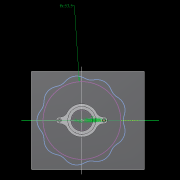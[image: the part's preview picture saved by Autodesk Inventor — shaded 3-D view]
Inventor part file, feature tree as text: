
AUTODESK INVENTOR PART (.ipt)
format: ipt  version: 2022.2 (Build 262287010, 287A)  size: 509,440 bytes
history: native  units: mm
features: other x19, extrude x14, sketch x9, pattern_circular x7, fillet x2, move_body x2, revolve x2, draft x2, plane x2
ambient origin geometry x8: Origin, YZ Plane, XZ Plane, XY Plane, X Axis, Y Axis, Z Axis, Center Point
bodies: Solid5 (feature_tree)
feature tree (59):
  other  "CrossSection1"
  sketch  "Sketch7"  dims[d90=16.297397mm]
  other  "Roller1"
  other  "Roller2"
  sketch  "Sketch22"  dims[d167=8.972256mm]
  sketch  "Sketch2"  dims[d57=4.025mm]
  sketch  "Sketch23"  dims[d173=10.814812mm]
  other  "RevRoller1"
  fillet  "Fillet1"  Radius=13.856406mm
  pattern_circular  "Circular Pattern13"  Count=360  [1 undecoded]
  move_body  "Move Body7"
  revolve  "Revolution13"  [1 undecoded]
  fillet  "Fillet3"  Radius=0.025mm
  pattern_circular  "Circular Pattern14"  [2 undecoded]
  move_body  "Move Body6"
  revolve  "Revolution14"  [1 undecoded]
  other  "OuterRim_Top2"
  other  "OuterRim_Bottom2"
  extrude  "Extrusion9"  Depth=12.0mm
  draft  "FaceDraft2"
  sketch  "Sketch30"  dims[d201=53.5mm d232=0.0mm d233=3600.0mm]
  plane  "Work Plane5"
  other  "Rotor Featurs"
  other  "RotorRim_Bottom"
  extrude  "Extrusion24"  Depth=12.0mm
  extrude  "Extrusion25"  Depth=0.1mm
  extrude  "Extrusion26"  Depth=12.0mm
  pattern_circular  "Circular Pattern23"  [2 undecoded]
  sketch  "Sketch41"  dims[d346=0.025mm]
  extrude  "Extrusion27"  Depth=12.0mm
  extrude  "Extrusion28"  TaperAngle=90.0deg  [1 undecoded]
  extrude  "Extrusion29"  Depth=12.0mm
  extrude  "Extrusion30"  Depth=12.0mm
  extrude  "Extrusion31"  TaperAngle=360.0deg  [1 undecoded]
  pattern_circular  "Circular Pattern24"  Angle=30.0deg  [1 undecoded]
  pattern_circular  "Circular Pattern25"  [2 undecoded]
  sketch  "Sketch42"  dims[d347=0.1mm]
  extrude  "Extrusion32"  Depth=12.0mm
  extrude  "Extrusion33"  Depth=0.1mm
  extrude  "Extrusion34"  Depth=12.0mm
  extrude  "Extrusion35"  TaperAngle=30.0deg  [1 undecoded]
  pattern_circular  "Circular Pattern26"  Angle=90.0deg  [1 undecoded]
  pattern_circular  "Circular Pattern27"  [2 undecoded]
  draft  "FaceDraft3"
  plane  "Work Plane6"
  extrude  "Extrusion36"  Depth=12.0mm
  other  "2D Equation Curve1"
  sketch  "Sketch40"  dims[d343=17.323467mm d344=17.325559mm d345=0.025mm]
  other  "Work Axis6"
  other  "Work Axis7"
  other  "Work Axis8"
  other  "Work Axis9"
  other  "Work Axis10"
  other  "Work Point1"
  other  "Work Point2"
  other  "Work Point3"
  other  "Work Point4"
  other  "Work Point5"
  sketch  "Sketch43"  dims[d348=0.1mm d349=17.325559mm d350=17.323467mm d351=0.025mm d352=0.025mm d354=0.1mm d355=17.323467mm d356=17.325559mm d357=1.0mm d358=90.0deg d359=0.5mm d360=60.0mm d361=360.0deg d363=30.0deg d367=8.1mm d369=4.014775mm d370=0.1mm d371=1.0mm d372=30.0deg d373=90.0deg d374=0.5mm d375=60.0mm d376=360.0deg d378=90.0deg d379=0.1mm d380=0.1mm d381=0.1mm d382=0.1mm d383=0.1mm d384=10.492204mm d385=0.0mm d386=0.0mm d391=1.0mm d392=53.5mm d393=1.5mm d394=1.5mm d395=1.5mm d396=1.5mm d397=90.0deg d398=90.0deg d399=90.0deg d400=53.5mm d401=10.492204mm d402=0.0mm d486=0.436332mm d487=0.5mm d488=2.0mm d489=0.0mm d490=20.0mm d495=2.5mm d496=8.0mm d506=13.856406mm d507=55.5mm d508=8.0mm d509=0.05mm d510=2.5mm d511=30.0deg d512=12.0mm d513=6.0mm d514=0.2mm d515=30.0deg d516=131.0mm d517=65.5mm d518=0.2mm d519=100.0mm d520=120.0mm d521=2.0mm d522=150.0mm d530=50.0mm d531=5.5mm d532=5.5mm d533=5.5mm d534=85.75mm d535=73.5mm d536=61.25mm d537=24.5mm d538=3.0mm d539=3.0mm d540=0.0mm d541=0.0mm d542=0.0mm d543=5.0mm d544=3.0mm d545=0.0mm d546=90.0mm d547=360.0deg d549=3.0mm d550=3.0mm d551=2.4mm d552=0.0mm d553=5.246102mm d554=0.0mm d555=2.4mm d556=0.0mm d557=5.246102mm d558=0.0mm d559=5.246102mm d560=0.0mm d561=90.0mm d562=360.0deg d564=60.0mm d565=360.0deg d567=5.0mm d568=5.0mm d569=3.0mm d570=0.0mm d571=5.246102mm d572=0.0mm d573=3.0mm d574=0.0mm d575=5.246102mm d576=0.0mm d577=90.0mm d578=360.0deg d580=60.0mm d581=360.0deg d583=0.436332mm d584=20.0mm d585=8.0mm d587=1.75mm d589=3.0mm d592=2.0mm d593=12.0mm d594=12.0mm d595=0.0mm d596=0.0mm d597=3.0mm d598=12.0mm d599=12.0mm d16=0.872665mm d17=0.872665mm d49=0.872665mm d50=0.872665mm d51=0.872665mm d52=0.872665mm d236=0.5mm d237=0.872665mm d238=0.5mm d239=0.872665mm d282=1.0mm d283=1.0mm d284=1.0mm d285=0.15mm d286=0.25mm d287=0.375mm d288=14.3117mm d289=0.75mm d290=20.594885mm d291=0.0625mm d292=0.75mm d293=0.375mm d405=0.5mm d406=0.872665mm d407=0.5mm d408=0.872665mm d413=0.5mm d414=0.872665mm d415=0.5mm d416=0.872665mm d417=0.5mm d418=0.872665mm d419=0.5mm d420=0.872665mm d421=0.872665mm d431=0.5mm d432=0.872665mm d433=0.5mm d434=0.872665mm d471=0.5mm d472=0.872665mm d473=0.5mm d474=0.872665mm d497=0.5mm d498=0.872665mm d499=0.5mm d500=0.872665mm d590=0.5mm d591=0.872665mm]
note: 16 required parameter values undecoded (feature->parameter linkage not recoverable at this tier; creation-order binding heuristic only, values carry confidence <= 0.55)